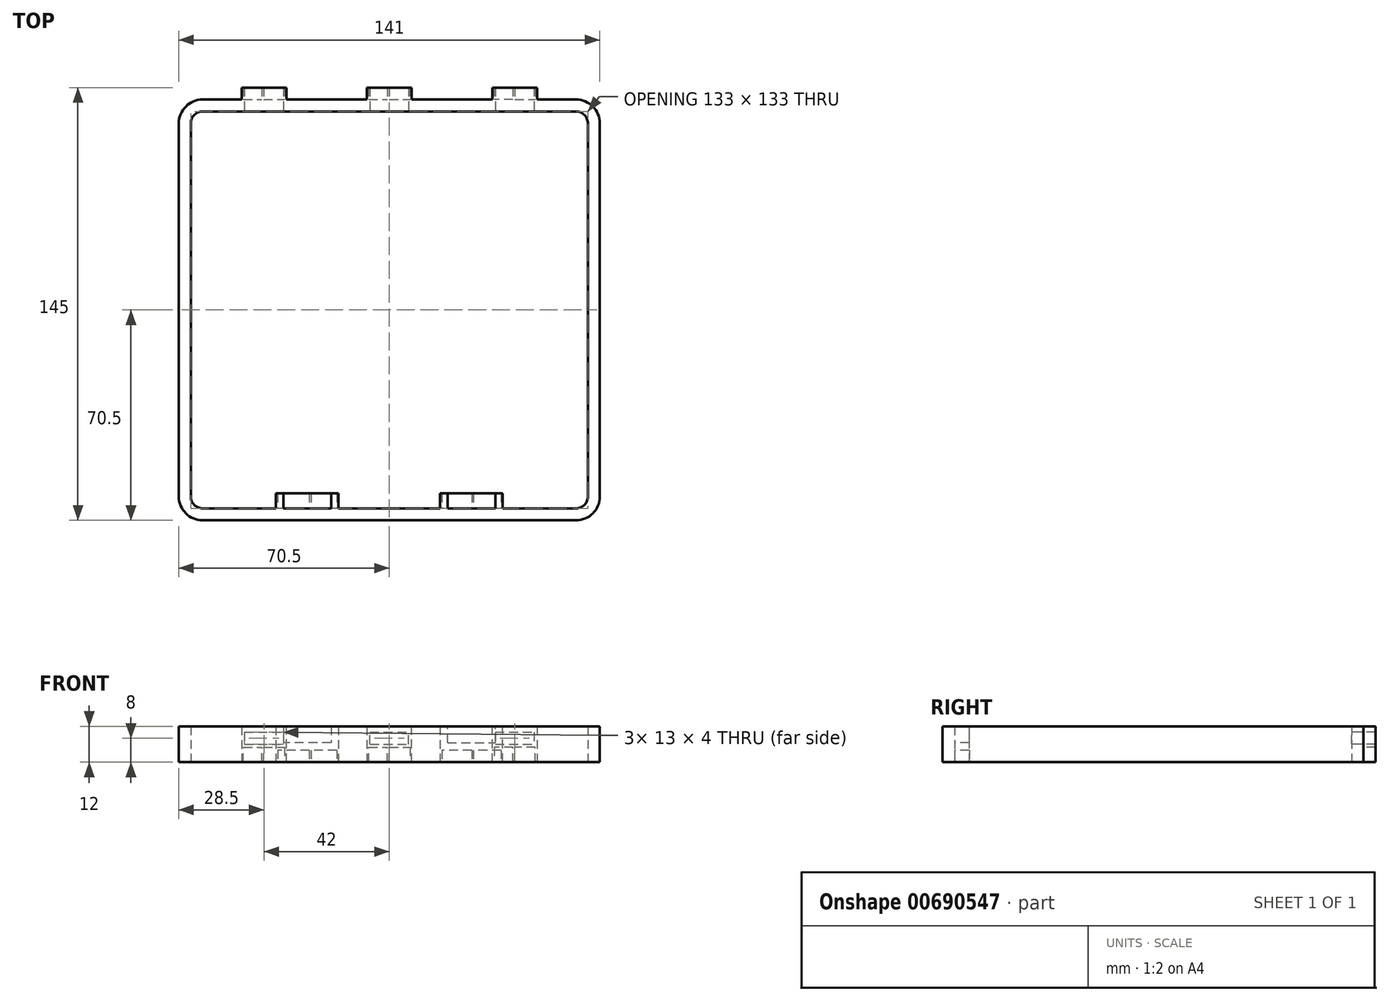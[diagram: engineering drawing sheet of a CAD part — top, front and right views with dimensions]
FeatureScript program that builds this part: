
annotation { "Feature Type Name" : "Feature", "Feature Type Description" : "" }
export const myFeature = defineFeature(function(context is Context, id is Id, definition is map)
    precondition{}
    {
        {
            var Q0;
            Q0=qCreatedBy(makeId("Top.planeOp"),FACE);
            var sketch = newSketch(context, id + "F0", { "sketchPlane" : qUnion([Q0])});
            skLineSegment(sketch, "E0.bottom", {"start": v(-61, -64.4) * mm, "end": v(64, -64.4) * mm});
            skLineSegment(sketch, "E0.top", {"start": v(-61, 68.6) * mm, "end": v(64, 68.6) * mm});
            skLineSegment(sketch, "E0.left", {"start": v(-65, -60.4) * mm, "end": v(-65, 64.6) * mm});
            skLineSegment(sketch, "E0.right", {"start": v(68, -60.4) * mm, "end": v(68, 64.6) * mm});
            skPoint(sketch, "E1.visualSharp", {"position": v(-65, 68.6) * mm});
            skArc(sketch, "E1.filletArc", {"start": v(-61, 68.6) * mm, "mid": v(-63.83, 67.43) * mm, "end": v(-65, 64.6) * mm});
            skPoint(sketch, "E2.visualSharp", {"position": v(68, 68.6) * mm});
            skArc(sketch, "E2.filletArc", {"start": v(68, 64.6) * mm, "mid": v(66.83, 67.43) * mm, "end": v(64, 68.6) * mm});
            skPoint(sketch, "E3.visualSharp", {"position": v(68, -64.4) * mm});
            skArc(sketch, "E3.filletArc", {"start": v(64, -64.4) * mm, "mid": v(66.83, -63.23) * mm, "end": v(68, -60.4) * mm});
            skPoint(sketch, "E4.visualSharp", {"position": v(-65, -64.4) * mm});
            skArc(sketch, "E4.filletArc", {"start": v(-65, -60.4) * mm, "mid": v(-63.83, -63.23) * mm, "end": v(-61, -64.4) * mm});
            skArc(sketch, "E5.0", {"start": v(-61, 72.6) * mm, "mid": v(-66.66, 70.26) * mm, "end": v(-69, 64.6) * mm});
            skLineSegment(sketch, "E5.1", {"start": v(-69, -60.4) * mm, "end": v(-69, 64.6) * mm});
            skLineSegment(sketch, "E5.2", {"start": v(-61, 72.6) * mm, "end": v(64, 72.6) * mm});
            skArc(sketch, "E5.3", {"start": v(-69, -60.4) * mm, "mid": v(-66.66, -66.06) * mm, "end": v(-61, -68.4) * mm});
            skArc(sketch, "E5.4", {"start": v(72, 64.6) * mm, "mid": v(69.66, 70.26) * mm, "end": v(64, 72.6) * mm});
            skLineSegment(sketch, "E5.5", {"start": v(72, -60.4) * mm, "end": v(72, 64.6) * mm});
            skArc(sketch, "E5.6", {"start": v(64, -68.4) * mm, "mid": v(69.66, -66.06) * mm, "end": v(72, -60.4) * mm});
            skLineSegment(sketch, "E5.7", {"start": v(-61, -68.4) * mm, "end": v(64, -68.4) * mm});
            skSolve(sketch);
        }
        {
            var Q0;
            Q0=makeQuery(id+"F0.imprint","IMPRINT",FACE,{"disambiguationData":[TD([[makeQuery(id+"F0.imprint","IMPRINT",EDGE,{"derivedFrom":sQuery(id+"F0.wireOp",EDGE,"E0.bottom")}),-1.0]])]});
            extrude(context, id + "F1", {"entities" : qUnion([Q0]), "depth" : 12 * mm, "offsetDistance" : 25 * mm});
        }
        {
            var Q0;
            Q0=makeQuery(id+"F1.opExtrude","SWEPT_FACE",FACE,{"disambiguationData":[OSD([sQuery(id+"F0.wireOp",EDGE,"E0.top")])]});
            var sketch = newSketch(context, id + "F2", { "sketchPlane" : qUnion([Q0])});
            skLineSegment(sketch, "E6", {"start": v(-65, 6) * mm, "end": v(-48, 6) * mm, "construction": true});
            skPoint(sketch, "E7", {"position": v(1.5, 6) * mm});
            skLineSegment(sketch, "E8", {"start": v(1.5, 6) * mm, "end": v(1.5, 0) * mm, "construction": true});
            skLineSegment(sketch, "E9.bottom", {"start": v(-5, 6) * mm, "end": v(8, 6) * mm});
            skLineSegment(sketch, "E9.top", {"start": v(-5, 10) * mm, "end": v(8, 10) * mm});
            skLineSegment(sketch, "E9.left", {"start": v(-5, 6) * mm, "end": v(-5, 10) * mm});
            skLineSegment(sketch, "E9.right", {"start": v(8, 6) * mm, "end": v(8, 10) * mm});
            skPoint(sketch, "E10", {"position": v(1.5, 10) * mm});
            skLineSegment(sketch, "E11.bottom", {"start": v(-47, 10) * mm, "end": v(-34, 10) * mm});
            skLineSegment(sketch, "E11.top", {"start": v(-47, 6) * mm, "end": v(-34, 6) * mm});
            skLineSegment(sketch, "E11.left", {"start": v(-47, 10) * mm, "end": v(-47, 6) * mm});
            skLineSegment(sketch, "E11.right", {"start": v(-34, 10) * mm, "end": v(-34, 6) * mm});
            skLineSegment(sketch, "E12.bottom", {"start": v(37, 10) * mm, "end": v(50, 10) * mm});
            skLineSegment(sketch, "E12.top", {"start": v(37, 6) * mm, "end": v(50, 6) * mm});
            skLineSegment(sketch, "E12.left", {"start": v(37, 10) * mm, "end": v(37, 6) * mm});
            skLineSegment(sketch, "E12.right", {"start": v(50, 10) * mm, "end": v(50, 6) * mm});
            skLineSegment(sketch, "E13.bottom", {"start": v(8, 6) * mm, "end": v(-5, 6) * mm});
            skLineSegment(sketch, "E14.bottom", {"start": v(-34, 6) * mm, "end": v(-47, 6) * mm});
            skLineSegment(sketch, "E15.trimOffspring", {"start": v(-47, 6) * mm, "end": v(-34, 6) * mm, "construction": true});
            skLineSegment(sketch, "E16.trimOffspring", {"start": v(-48, 6) * mm, "end": v(-6, 6) * mm, "construction": true});
            skLineSegment(sketch, "E17.trimOffspring", {"start": v(9, 6) * mm, "end": v(51, 6) * mm, "construction": true});
            skLineSegment(sketch, "E18.trimOffspring", {"start": v(-5, 6) * mm, "end": v(8, 6) * mm, "construction": true});
            skLineSegment(sketch, "E19.trimOffspring", {"start": v(51, 6) * mm, "end": v(68, 6) * mm, "construction": true});
            skLineSegment(sketch, "E20.trimOffspring", {"start": v(37, 6) * mm, "end": v(50, 6) * mm, "construction": true});
            skLineSegment(sketch, "E21", {"start": v(-48, 6) * mm, "end": v(-48, 12) * mm});
            skLineSegment(sketch, "E22", {"start": v(-48, 12) * mm, "end": v(-33, 12) * mm});
            skLineSegment(sketch, "E23", {"start": v(-33, 12) * mm, "end": v(-33, 0) * mm});
            skLineSegment(sketch, "E24", {"start": v(-33, 0) * mm, "end": v(-33.6, 0) * mm});
            skLineSegment(sketch, "E25", {"start": v(-33.6, 0) * mm, "end": v(-33.6, 5) * mm});
            skLineSegment(sketch, "E26", {"start": v(-33.6, 5) * mm, "end": v(-40.6, 5) * mm});
            skLineSegment(sketch, "E27", {"start": v(-47.4, 5) * mm, "end": v(-47.4, 0) * mm});
            skLineSegment(sketch, "E28", {"start": v(-47.4, 0) * mm, "end": v(-48, 0) * mm});
            skLineSegment(sketch, "E29", {"start": v(-48, 0) * mm, "end": v(-48, 6) * mm});
            skLineSegment(sketch, "E30", {"start": v(-6, 6) * mm, "end": v(-6, 12) * mm});
            skLineSegment(sketch, "E31", {"start": v(-6, 12) * mm, "end": v(9, 12) * mm});
            skLineSegment(sketch, "E32", {"start": v(9, 12) * mm, "end": v(9, 0) * mm});
            skLineSegment(sketch, "E33", {"start": v(9, 0) * mm, "end": v(8.4, 0) * mm});
            skLineSegment(sketch, "E34", {"start": v(8.4, 0) * mm, "end": v(8.4, 5) * mm});
            skLineSegment(sketch, "E35", {"start": v(8.4, 5) * mm, "end": v(1.5, 5) * mm});
            skLineSegment(sketch, "E36", {"start": v(-5.4, 5) * mm, "end": v(-5.4, 0) * mm});
            skLineSegment(sketch, "E37", {"start": v(-5.4, 0) * mm, "end": v(-6, 0) * mm});
            skLineSegment(sketch, "E38", {"start": v(-6, 0) * mm, "end": v(-6, 6) * mm});
            skLineSegment(sketch, "E39", {"start": v(51, 6) * mm, "end": v(51, 12) * mm});
            skLineSegment(sketch, "E40", {"start": v(51, 12) * mm, "end": v(36, 12) * mm});
            skLineSegment(sketch, "E41", {"start": v(36, 12) * mm, "end": v(36, 0) * mm});
            skLineSegment(sketch, "E42", {"start": v(36, 0) * mm, "end": v(36.6, 0) * mm});
            skLineSegment(sketch, "E43", {"start": v(36.6, 0) * mm, "end": v(36.6, 5) * mm});
            skLineSegment(sketch, "E44", {"start": v(36.6, 5) * mm, "end": v(42.9, 5) * mm});
            skLineSegment(sketch, "E45", {"start": v(50.4, 5) * mm, "end": v(50.4, 0) * mm});
            skLineSegment(sketch, "E46", {"start": v(50.4, 0) * mm, "end": v(51, 0) * mm});
            skLineSegment(sketch, "E47", {"start": v(51, 0) * mm, "end": v(51, 6) * mm});
            skLineSegment(sketch, "E48.top", {"start": v(43.5, 0) * mm, "end": v(42.9, 0) * mm});
            skLineSegment(sketch, "E48.left", {"start": v(43.5, 5) * mm, "end": v(43.5, 0) * mm});
            skLineSegment(sketch, "E48.right", {"start": v(42.9, 5) * mm, "end": v(42.9, 0) * mm});
            skLineSegment(sketch, "E49.top", {"start": v(1.5, 0) * mm, "end": v(0.9, 0) * mm});
            skLineSegment(sketch, "E49.left", {"start": v(1.5, 5) * mm, "end": v(1.5, 0) * mm});
            skLineSegment(sketch, "E49.right", {"start": v(0.9, 5) * mm, "end": v(0.9, 0) * mm});
            skLineSegment(sketch, "E50.top", {"start": v(-40.6, 0) * mm, "end": v(-41.2, 0) * mm});
            skLineSegment(sketch, "E50.left", {"start": v(-40.6, 5) * mm, "end": v(-40.6, 0) * mm});
            skLineSegment(sketch, "E50.right", {"start": v(-41.2, 5) * mm, "end": v(-41.2, 0) * mm});
            skLineSegment(sketch, "E51.trimOffspring", {"start": v(-41.2, 5) * mm, "end": v(-47.4, 5) * mm});
            skLineSegment(sketch, "E52.trimOffspring", {"start": v(0.9, 5) * mm, "end": v(-5.4, 5) * mm});
            skLineSegment(sketch, "E53.trimOffspring", {"start": v(43.5, 5) * mm, "end": v(50.4, 5) * mm});
            skSolve(sketch);
        }
        {
            var Q0;
            Q0=makeQuery(id+"F2.imprint","IMPRINT",FACE,{"disambiguationData":[TD([[makeQuery(id+"F2.imprint","IMPRINT",EDGE,{"derivedFrom":sQuery(id+"F2.wireOp",EDGE,"E11.bottom")}),1.0]])]});
            var Q1;
            Q1=makeQuery(id+"F2.imprint","IMPRINT",FACE,{"disambiguationData":[TD([[makeQuery(id+"F2.imprint","IMPRINT",EDGE,{"derivedFrom":sQuery(id+"F2.wireOp",EDGE,"E9.top")}),1.0]])]});
            var Q2;
            Q2=makeQuery(id+"F2.imprint","IMPRINT",FACE,{"disambiguationData":[TD([[makeQuery(id+"F2.imprint","IMPRINT",EDGE,{"derivedFrom":sQuery(id+"F2.wireOp",EDGE,"E12.bottom")}),1.0]])]});
            extrude(context, id + "F3", {"entities" : qUnion([Q0, Q1, Q2]), "operationType" : NewBodyOperationType.ADD, "oppositeDirection" : true, "depth" : 8 * mm, "offsetDistance" : 25 * mm});
        }
        {
            var Q0;
            Q0=makeQuery(id+"F2.imprint","IMPRINT",FACE,{"disambiguationData":[TD([[makeQuery(id+"F2.imprint","IMPRINT",EDGE,{"derivedFrom":sQuery(id+"F2.wireOp",EDGE,"E12.bottom")}),-1.0]])]});
            var Q1;
            Q1=makeQuery(id+"F2.imprint","IMPRINT",FACE,{"disambiguationData":[TD([[makeQuery(id+"F2.imprint","IMPRINT",EDGE,{"derivedFrom":sQuery(id+"F2.wireOp",EDGE,"E9.top")}),-1.0]])]});
            var Q2;
            Q2=makeQuery(id+"F2.imprint","IMPRINT",FACE,{"disambiguationData":[TD([[makeQuery(id+"F2.imprint","IMPRINT",EDGE,{"derivedFrom":sQuery(id+"F2.wireOp",EDGE,"E11.bottom")}),-1.0]])]});
            extrude(context, id + "F4", {"entities" : qUnion([Q0, Q1, Q2]), "operationType" : NewBodyOperationType.REMOVE, "oppositeDirection" : true, "depth" : 25 * mm, "offsetDistance" : 25 * mm});
        }
        {
            var Q0;
            Q0=makeQuery(id+"F1.opExtrude","SWEPT_FACE",FACE,{"disambiguationData":[OSD([sQuery(id+"F0.wireOp",EDGE,"E0.bottom")])]});
            var sketch = newSketch(context, id + "F5", { "sketchPlane" : qUnion([Q0])});
            skLineSegment(sketch, "E54", {"start": v(-66.5, 4) * mm, "end": v(-39.5, 4) * mm, "construction": true});
            skPoint(sketch, "E55", {"position": v(-1.5, 4) * mm});
            skLineSegment(sketch, "E56", {"start": v(-1.5, 4) * mm, "end": v(-1.5, 0) * mm, "construction": true});
            skLineSegment(sketch, "E57.top", {"start": v(-18.5, 12) * mm, "end": v(-21, 12) * mm});
            skLineSegment(sketch, "E57.left", {"start": v(-18.5, 4) * mm, "end": v(-18.5, 12) * mm});
            skLineSegment(sketch, "E57.right", {"start": v(-39.5, 4) * mm, "end": v(-39.5, 12) * mm});
            skLineSegment(sketch, "E58.bottom", {"start": v(15.5, 12) * mm, "end": v(18, 12) * mm});
            skLineSegment(sketch, "E58.left", {"start": v(15.5, 12) * mm, "end": v(15.5, 4) * mm});
            skLineSegment(sketch, "E58.right", {"start": v(36.5, 12) * mm, "end": v(36.5, 4) * mm});
            skLineSegment(sketch, "E59.trimOffspring", {"start": v(-18.5, 4) * mm, "end": v(15.5, 4) * mm, "construction": true});
            skLineSegment(sketch, "E60.trimOffspring", {"start": v(36.5, 4) * mm, "end": v(63.5, 4) * mm, "construction": true});
            skLineSegment(sketch, "E61.0", {"start": v(-37, 6.5) * mm, "end": v(-37, 12) * mm});
            skLineSegment(sketch, "E61.1", {"start": v(-21, 6.5) * mm, "end": v(-37, 6.5) * mm});
            skLineSegment(sketch, "E61.2", {"start": v(-21, 6.5) * mm, "end": v(-21, 12) * mm});
            skLineSegment(sketch, "E62.0", {"start": v(34, 12) * mm, "end": v(34, 6.5) * mm});
            skLineSegment(sketch, "E62.1", {"start": v(18, 6.5) * mm, "end": v(34, 6.5) * mm});
            skLineSegment(sketch, "E62.2", {"start": v(18, 12) * mm, "end": v(18, 6.5) * mm});
            skLineSegment(sketch, "E63.trimOffspring", {"start": v(34, 12) * mm, "end": v(36.5, 12) * mm});
            skLineSegment(sketch, "E64.trimOffspring", {"start": v(-37, 12) * mm, "end": v(-39.5, 12) * mm});
            skLineSegment(sketch, "E65.left", {"start": v(-18.5, 4) * mm, "end": v(-18.5, 4) * mm});
            skLineSegment(sketch, "E65.right", {"start": v(-39.5, 4) * mm, "end": v(-39.5, 4) * mm});
            skLineSegment(sketch, "E66.top", {"start": v(-39.5, 0) * mm, "end": v(-38.9, 0) * mm});
            skLineSegment(sketch, "E66.left", {"start": v(-39.5, 4) * mm, "end": v(-39.5, 0) * mm});
            skLineSegment(sketch, "E66.right", {"start": v(-18.5, 4) * mm, "end": v(-18.5, 0) * mm});
            skLineSegment(sketch, "E67.bottom", {"start": v(16.1, 4) * mm, "end": v(24.7, 4) * mm});
            skLineSegment(sketch, "E67.top", {"start": v(15.5, 0) * mm, "end": v(16.1, 0) * mm});
            skLineSegment(sketch, "E67.left", {"start": v(15.5, 4) * mm, "end": v(15.5, 0) * mm});
            skLineSegment(sketch, "E67.right", {"start": v(36.5, 4) * mm, "end": v(36.5, 0) * mm});
            skLineSegment(sketch, "E68.0", {"start": v(16.1, 4) * mm, "end": v(16.1, 0) * mm});
            skLineSegment(sketch, "E69.0", {"start": v(35.9, 4) * mm, "end": v(35.9, 0) * mm});
            skLineSegment(sketch, "E70.trimOffspring", {"start": v(35.9, 0) * mm, "end": v(36.5, 0) * mm});
            skLineSegment(sketch, "E71.0", {"start": v(-19.1, 4) * mm, "end": v(-19.1, 0) * mm});
            skLineSegment(sketch, "E72.0", {"start": v(-38.9, 4) * mm, "end": v(-38.9, 0) * mm});
            skLineSegment(sketch, "E73.trimOffspring", {"start": v(-19.1, 0) * mm, "end": v(-18.5, 0) * mm});
            skLineSegment(sketch, "E74", {"start": v(-38.9, 4) * mm, "end": v(-29.7, 4) * mm});
            skLineSegment(sketch, "E75.top", {"start": v(25.3, 0) * mm, "end": v(24.7, 0) * mm});
            skLineSegment(sketch, "E75.left", {"start": v(25.3, 4) * mm, "end": v(25.3, 0) * mm});
            skLineSegment(sketch, "E75.right", {"start": v(24.7, 4) * mm, "end": v(24.7, 0) * mm});
            skLineSegment(sketch, "E76.top", {"start": v(-29.7, 0) * mm, "end": v(-29.1, 0) * mm});
            skLineSegment(sketch, "E76.left", {"start": v(-29.7, 4) * mm, "end": v(-29.7, 0) * mm});
            skLineSegment(sketch, "E76.right", {"start": v(-29.1, 4) * mm, "end": v(-29.1, 0) * mm});
            skLineSegment(sketch, "E77.trimOffspring", {"start": v(-29.1, 4) * mm, "end": v(-19.1, 4) * mm});
            skLineSegment(sketch, "E78.trimOffspring", {"start": v(25.3, 4) * mm, "end": v(35.9, 4) * mm});
            skSolve(sketch);
        }
        {
            var Q0;
            Q0=makeQuery(id+"F5.imprint","IMPRINT",FACE,{"disambiguationData":[TD([[makeQuery(id+"F5.imprint","IMPRINT",EDGE,{"derivedFrom":sQuery(id+"F5.wireOp",EDGE,"E57.top")}),1.0]])]});
            var Q1;
            Q1=makeQuery(id+"F5.imprint","IMPRINT",FACE,{"disambiguationData":[TD([[makeQuery(id+"F5.imprint","IMPRINT",EDGE,{"derivedFrom":sQuery(id+"F5.wireOp",EDGE,"E58.bottom")}),1.0]])]});
            extrude(context, id + "F6", {"entities" : qUnion([Q0, Q1]), "operationType" : NewBodyOperationType.ADD, "depth" : 5 * mm, "offsetDistance" : 25 * mm});
        }
    });
